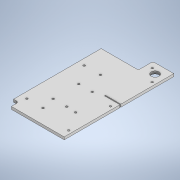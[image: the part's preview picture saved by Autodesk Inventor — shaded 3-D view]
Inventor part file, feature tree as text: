
AUTODESK INVENTOR PART (.ipt)
format: ipt  version: 2021 (Build 250183000, 183)  size: 208,384 bytes
history: native  units: mm
features: sketch x6, hole x4, extrude x3, fillet x1, projected_geometry x1
ambient origin geometry x8: Origin, YZ Plane, XZ Plane, XY Plane, X Axis, Y Axis, Z Axis, Center Point
bodies: Solid1 (feature_tree)
feature tree (15):
  extrude  "Extrusion1"  Depth=210.0mm
  hole  "Hole1"  [1 undecoded]
  hole  "Hole2"  [1 undecoded]
  hole  "Hole5"  [1 undecoded]
  extrude  "Extrusion9"  Depth=29.7mm
  hole  "Hole6"  [1 undecoded]
  extrude  "Extrusion10"  Depth=0.5mm
  fillet  "Fillet1"  Radius=90.0mm
  sketch  "Sketch1"  dims[d0=111.2mm d1=210.0mm]
  sketch  "Sketch6"  dims[d2=5.0mm d3=0.0mm d6=31.0mm]
  sketch  "Sketch13"  dims[d7=31.0mm]
  projected_geometry  "Projected Loop2"
  sketch  "Sketch14"  dims[d8=3.8mm d9=6.0mm d10=4.0mm d11=2.0mm d12=90.0deg d13=8.0mm d14=20.594885mm d17=12.0mm]
  sketch  "Sketch15"  dims[d18=12.0mm d29=68.0mm]
  sketch  "Sketch16"  dims[d30=147.0mm d32=29.7mm d33=3.8mm d34=6.0mm d35=4.0mm d36=2.0mm d37=90.0deg d38=8.0mm d39=20.594885mm d75=1.8mm d76=0.5mm d77=90.0mm d78=57.0mm d79=0.0mm d80=0.0mm d84=10.0mm d85=40.0mm d86=14.0mm d87=10.0mm d88=4.0mm d89=110.0mm d90=27.5mm d91=51.5mm d92=11.5mm d93=6.5mm d94=15.0mm d95=80.0mm d96=80.0mm d97=3.8mm d98=6.0mm d99=4.0mm d100=2.0mm d101=90.0deg d102=8.0mm d103=20.594885mm d104=26.0mm d105=49.0mm d106=25.0mm d107=18.0mm d108=3.8mm d109=6.0mm d110=4.0mm d111=2.0mm d112=90.0deg d113=8.0mm d114=20.594885mm d115=18.0mm d116=15.0mm d117=18.7mm d118=17.1mm d119=0.0mm d120=0.0mm d121=4.0mm]
note: 4 required parameter values undecoded (feature->parameter linkage not recoverable at this tier; creation-order binding heuristic only, values carry confidence <= 0.55)
